# Revit family: Block 2100
name_source: partatom
category: Оборудование
units: mm (PartAtom-declared; Revit-internal decimal feet)

## family parameters
Всегда вертикально = Да
Классификация = Нет
На основе рабочей плоскости = Нет
Общий = Нет
При загрузке вырезать с полостями = Нет
Размер круглого соединителя = Использовать диаметр
Тип детали = Нормальный
Точка расчета площади = Нет

## types (1)
- Block 2100
    A1 длина = 1200 мм
    ADSK_Единица измерения = шт.
    ADSK_Завод-изготовитель = ООО «Турков»
    ADSK_Количество фаз = 1
    ADSK_Марка = Block 2100
    ADSK_Масса = 0
    ADSK_Наименование = Канальный очиститель с высокой степенью фильтрации Block
    ADSK_Напряжение = 220 В
    ADSK_Номинальная мощность = 750 Вт
    ADSK_Расход воздуха = 1600.0 м³/ч
    ADSK_Свободный напор воздуха = 522.0 Па
    ADSK_Ток = 3 А
    B1 глубина = 440 мм
    C1 высота = 660 мм
    ВВ_Дл = 500 мм
    ВВ_Шир = 250 мм
    ВВ_толщ = 45 мм
    КА_y = 45 мм
    КА_высота = 100 мм
    КА_толщина = 50 мм
    КА_ширина = 100 мм
    Кол-во вентиляторов = 1
    СЗ = 500 мм
    СЗ КА = Да
    УГО = 330 мм
    Угол УГО = 19.80°

## geometry (parser evidence)
native form markers: Sweep x6
no freeform markers — native parametric forms only
